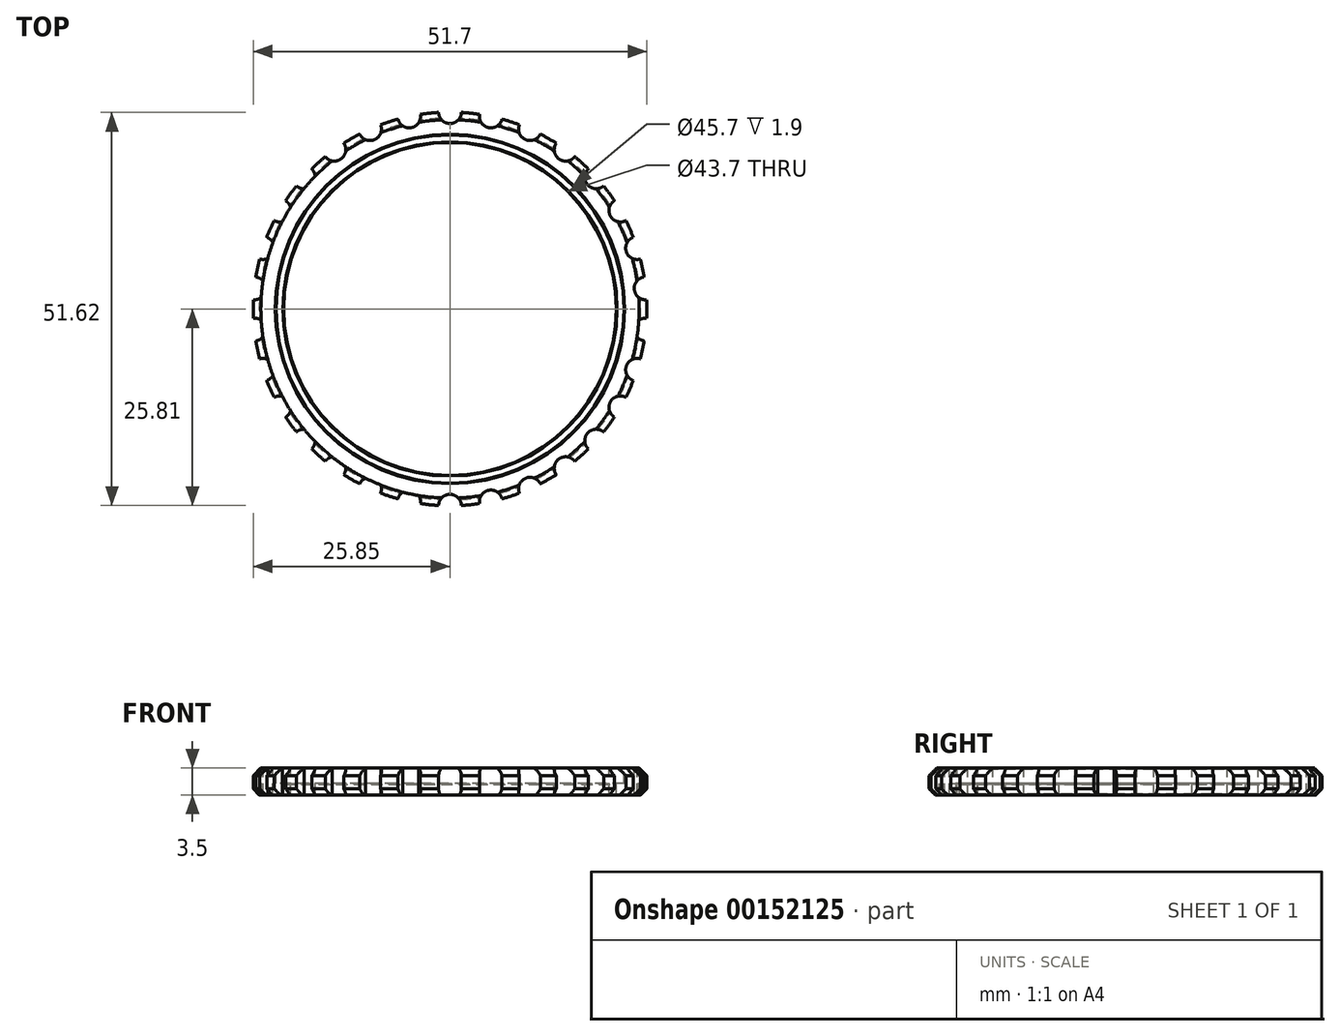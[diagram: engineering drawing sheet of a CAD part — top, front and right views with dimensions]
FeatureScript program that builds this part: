
annotation { "Feature Type Name" : "Feature", "Feature Type Description" : "" }
export const myFeature = defineFeature(function(context is Context, id is Id, definition is map)
    precondition{}
    {
        {
            var Q0;
            Q0=qCreatedBy(makeId("Front.planeOp"),FACE);
            var sketch = newSketch(context, id + "F0", { "sketchPlane" : qUnion([Q0])});
            skLineSegment(sketch, "E0.bottom", {"start": v(-22.85, -1) * mm, "end": v(22.85, -1) * mm, "construction": true});
            skLineSegment(sketch, "E0.top", {"start": v(-22.85, 1) * mm, "end": v(22.85, 1) * mm, "construction": true});
            skLineSegment(sketch, "E0.left", {"start": v(-22.85, -1) * mm, "end": v(-22.85, 1) * mm, "construction": true});
            skLineSegment(sketch, "E0.right", {"start": v(22.85, -1) * mm, "end": v(22.85, 1) * mm, "construction": true});
            skPoint(sketch, "E0.middle", {"position": v(0, 0) * mm});
            skLineSegment(sketch, "E1", {"start": v(-22.85, 1) * mm, "end": v(-25.85, 1) * mm});
            skLineSegment(sketch, "E2", {"start": v(-25.85, 1) * mm, "end": v(-25.85, -2.5) * mm});
            skLineSegment(sketch, "E3", {"start": v(-25.85, -2.5) * mm, "end": v(-21.85, -2.5) * mm});
            skLineSegment(sketch, "E4", {"start": v(-22.85, -1) * mm, "end": v(-21.85, -1) * mm});
            skLineSegment(sketch, "E5", {"start": v(-22.85, -1) * mm, "end": v(-22.85, 1) * mm});
            skLineSegment(sketch, "E6", {"start": v(-21.85, -1) * mm, "end": v(-21.85, -2.5) * mm});
            skLineSegment(sketch, "E7", {"start": v(0, 1) * mm, "end": v(0, -1) * mm, "construction": true});
            skSolve(sketch);
        }
        {
            var Q0;
            Q0=makeQuery(id+"F0.imprint","IMPRINT",FACE,{"disambiguationData":[TD([[makeQuery(id+"F0.imprint","IMPRINT",EDGE,{"derivedFrom":sQuery(id+"F0.wireOp",EDGE,"E1")}),1.0]])]});
            var Q1;
            Q1=sQuery(id+"F0.wireOp",EDGE,"E7");
            revolve(context, id + "F1", {"entities" : qUnion([Q0]), "axis" : qUnion([Q1]), "revolveType" : RevolveType.FULL});
        }
        {
            var Q0;
            Q0=makeQuery(id+"F1.opRevolve","SWEPT_EDGE",EDGE,{"disambiguationData":[OSD([sQuery(id+"F0.wireOp",EDGE,"E1"),sQuery(id+"F0.wireOp",EDGE,"E2")])]});
            chamfer(context, id + "F2", {"entities" : qUnion([Q0]), "width" : 1 * mm, "tangentPropagation" : true});
        }
        {
            var Q0;
            Q0=makeQuery(id+"F1.opRevolve","SWEPT_EDGE",EDGE,{"disambiguationData":[OSD([sQuery(id+"F0.wireOp",EDGE,"E2"),sQuery(id+"F0.wireOp",EDGE,"E3")])]});
            chamfer(context, id + "F3", {"entities" : qUnion([Q0]), "width" : .8 * mm, "tangentPropagation" : true});
        }
        {
            var Q0;
            Q0=makeQuery(id+"F1.opRevolve","SWEPT_EDGE",EDGE,{"disambiguationData":[OSD([sQuery(id+"F0.wireOp",EDGE,"E1"),sQuery(id+"F0.wireOp",EDGE,"E5")])]});
            var Q1;
            Q1=makeQuery(id+"F1.opRevolve","SWEPT_EDGE",EDGE,{"disambiguationData":[OSD([sQuery(id+"F0.wireOp",EDGE,"E4"),sQuery(id+"F0.wireOp",EDGE,"E6")])]});
            var Q2;
            Q2=makeQuery(id+"F1.opRevolve","SWEPT_EDGE",EDGE,{"disambiguationData":[OSD([sQuery(id+"F0.wireOp",EDGE,"E3"),sQuery(id+"F0.wireOp",EDGE,"E6")])]});
            chamfer(context, id + "F4", {"entities" : qUnion([Q0, Q1, Q2]), "width" : .1 * mm, "tangentPropagation" : true});
        }
        {
            var Q0;
            Q0=makeQuery(id+"F1.opRevolve","SWEPT_FACE",FACE,{"disambiguationData":[OSD([sQuery(id+"F0.wireOp",EDGE,"E1")])]});
            var sketch = newSketch(context, id + "F5", { "sketchPlane" : qUnion([Q0])});
            skCircle(sketch, "E8.0", {"center": v(0, 0) * mm, "radius": 25.85 * mm});
            skLineSegment(sketch, "E9", {"start": v(0, 0) * mm, "end": v(0, 25.85) * mm, "construction": true});
            skCircle(sketch, "E10", {"center": v(0, 25.85) * mm, "radius": 1.5 * mm});
            skCircle(sketch, "E11.1.0", {"center": v(-5.37, 25.29) * mm, "radius": 1.5 * mm});
            skCircle(sketch, "E11.2.0", {"center": v(-10.51, 23.62) * mm, "radius": 1.5 * mm});
            skCircle(sketch, "E11.3.0", {"center": v(-15.2, 20.91) * mm, "radius": 1.5 * mm});
            skCircle(sketch, "E11.4.0", {"center": v(-19.21, 17.3) * mm, "radius": 1.5 * mm});
            skCircle(sketch, "E11.5.0", {"center": v(-22.39, 12.93) * mm, "radius": 1.5 * mm});
            skCircle(sketch, "E11.6.0", {"center": v(-24.58, 7.99) * mm, "radius": 1.5 * mm});
            skCircle(sketch, "E11.7.0", {"center": v(-25.7, 2.7) * mm, "radius": 1.5 * mm});
            skCircle(sketch, "E11.8.0", {"center": v(-25.7, -2.7) * mm, "radius": 1.5 * mm});
            skCircle(sketch, "E11.9.0", {"center": v(-24.58, -7.99) * mm, "radius": 1.5 * mm});
            skCircle(sketch, "E11.10.0", {"center": v(-22.39, -12.92) * mm, "radius": 1.5 * mm});
            skCircle(sketch, "E11.11.0", {"center": v(-19.21, -17.3) * mm, "radius": 1.5 * mm});
            skCircle(sketch, "E11.12.0", {"center": v(-15.2, -20.91) * mm, "radius": 1.5 * mm});
            skCircle(sketch, "E11.13.0", {"center": v(-10.51, -23.62) * mm, "radius": 1.5 * mm});
            skCircle(sketch, "E11.14.0", {"center": v(-5.37, -25.29) * mm, "radius": 1.5 * mm});
            skCircle(sketch, "E11.15.0", {"center": v(0, -25.85) * mm, "radius": 1.5 * mm});
            skCircle(sketch, "E11.16.0", {"center": v(5.37, -25.29) * mm, "radius": 1.5 * mm});
            skCircle(sketch, "E11.17.0", {"center": v(10.51, -23.62) * mm, "radius": 1.5 * mm});
            skCircle(sketch, "E11.18.0", {"center": v(15.2, -20.91) * mm, "radius": 1.5 * mm});
            skCircle(sketch, "E11.19.0", {"center": v(19.21, -17.3) * mm, "radius": 1.5 * mm});
            skCircle(sketch, "E11.20.0", {"center": v(22.39, -12.93) * mm, "radius": 1.5 * mm});
            skCircle(sketch, "E11.21.0", {"center": v(24.58, -7.99) * mm, "radius": 1.5 * mm});
            skCircle(sketch, "E11.22.0", {"center": v(25.7, -2.7) * mm, "radius": 1.5 * mm});
            skCircle(sketch, "E11.23.0", {"center": v(25.7, 2.7) * mm, "radius": 1.5 * mm});
            skCircle(sketch, "E11.24.0", {"center": v(24.58, 7.99) * mm, "radius": 1.5 * mm});
            skCircle(sketch, "E11.25.0", {"center": v(22.39, 12.93) * mm, "radius": 1.5 * mm});
            skCircle(sketch, "E11.26.0", {"center": v(19.21, 17.3) * mm, "radius": 1.5 * mm});
            skCircle(sketch, "E11.27.0", {"center": v(15.2, 20.91) * mm, "radius": 1.5 * mm});
            skCircle(sketch, "E11.28.0", {"center": v(10.51, 23.62) * mm, "radius": 1.5 * mm});
            skCircle(sketch, "E11.29.0", {"center": v(5.37, 25.29) * mm, "radius": 1.5 * mm});
            skSolve(sketch);
        }
        {
            var Q0;
            {var subQ0=sQuery(id+"F5.wireOp",EDGE,"E10");var subQ1=sQuery(id+"F5.wireOp",EDGE,"E8.0");var subQ2=makeQuery(id+"F5.imprint","INTERSECT",VERTEX,{"disambiguationData":[OD(0.0)],"derivedFrom":[subQ1,subQ0]});Q0=makeQuery(id+"F5.imprint","IMPRINT",FACE,{"disambiguationData":[TD([[makeQuery(id+"F5.imprint","IMPRINT",EDGE,{"disambiguationData":[TD([[subQ2,-1.0]])],"derivedFrom":subQ1}),1.0]])]});}
            var Q1;
            {var subQ0=sQuery(id+"F5.wireOp",EDGE,"E10");var subQ1=sQuery(id+"F0.wireOp",EDGE,"E1");var subQ2=makeQuery(id+"F2.opChamfer","BLEND_EDGE",EDGE,{"blendedFrom":[makeQuery(id+"F1.opRevolve","SWEPT_EDGE",EDGE,{"disambiguationData":[OSD([subQ1,sQuery(id+"F0.wireOp",EDGE,"E2")])]}),makeQuery(id+"F1.opRevolve","SWEPT_FACE",FACE,{"disambiguationData":[OSD([subQ1])]})],"blendedInto":[makeQuery(id+"F1.opRevolve","SWEPT_FACE",FACE,{"disambiguationData":[OSD([subQ1])]})]});var subQ3=makeQuery(id+"F5.imprint","INTERSECT",VERTEX,{"disambiguationData":[OD(0.0)],"derivedFrom":[subQ2,subQ0]});Q1=makeQuery(id+"F5.imprint","IMPRINT",FACE,{"disambiguationData":[TD([[makeQuery(id+"F5.imprint","IMPRINT",EDGE,{"disambiguationData":[TD([[subQ3,-1.0]])],"derivedFrom":subQ0}),1.0]])]});}
            var Q2;
            {var subQ0=sQuery(id+"F5.wireOp",EDGE,"E11.29.0");var subQ1=sQuery(id+"F5.wireOp",EDGE,"E8.0");var subQ2=makeQuery(id+"F5.imprint","INTERSECT",VERTEX,{"disambiguationData":[OD(0.0)],"derivedFrom":[subQ1,subQ0]});Q2=makeQuery(id+"F5.imprint","IMPRINT",FACE,{"disambiguationData":[TD([[makeQuery(id+"F5.imprint","IMPRINT",EDGE,{"disambiguationData":[TD([[subQ2,-1.0]])],"derivedFrom":subQ1}),1.0]])]});}
            var Q3;
            {var subQ0=sQuery(id+"F5.wireOp",EDGE,"E11.29.0");var subQ1=sQuery(id+"F0.wireOp",EDGE,"E1");var subQ2=makeQuery(id+"F2.opChamfer","BLEND_EDGE",EDGE,{"blendedFrom":[makeQuery(id+"F1.opRevolve","SWEPT_EDGE",EDGE,{"disambiguationData":[OSD([subQ1,sQuery(id+"F0.wireOp",EDGE,"E2")])]}),makeQuery(id+"F1.opRevolve","SWEPT_FACE",FACE,{"disambiguationData":[OSD([subQ1])]})],"blendedInto":[makeQuery(id+"F1.opRevolve","SWEPT_FACE",FACE,{"disambiguationData":[OSD([subQ1])]})]});var subQ3=makeQuery(id+"F5.imprint","INTERSECT",VERTEX,{"disambiguationData":[OD(0.0)],"derivedFrom":[subQ2,subQ0]});Q3=makeQuery(id+"F5.imprint","IMPRINT",FACE,{"disambiguationData":[TD([[makeQuery(id+"F5.imprint","IMPRINT",EDGE,{"disambiguationData":[TD([[subQ3,-1.0]])],"derivedFrom":subQ0}),1.0]])]});}
            var Q4;
            {var subQ0=sQuery(id+"F5.wireOp",EDGE,"E11.28.0");var subQ1=sQuery(id+"F5.wireOp",EDGE,"E8.0");var subQ2=makeQuery(id+"F5.imprint","INTERSECT",VERTEX,{"disambiguationData":[OD(0.0)],"derivedFrom":[subQ1,subQ0]});Q4=makeQuery(id+"F5.imprint","IMPRINT",FACE,{"disambiguationData":[TD([[makeQuery(id+"F5.imprint","IMPRINT",EDGE,{"disambiguationData":[TD([[subQ2,-1.0]])],"derivedFrom":subQ1}),1.0]])]});}
            var Q5;
            {var subQ0=sQuery(id+"F5.wireOp",EDGE,"E11.27.0");var subQ1=sQuery(id+"F5.wireOp",EDGE,"E8.0");var subQ2=makeQuery(id+"F5.imprint","INTERSECT",VERTEX,{"disambiguationData":[OD(0.0)],"derivedFrom":[subQ1,subQ0]});Q5=makeQuery(id+"F5.imprint","IMPRINT",FACE,{"disambiguationData":[TD([[makeQuery(id+"F5.imprint","IMPRINT",EDGE,{"disambiguationData":[TD([[subQ2,-1.0]])],"derivedFrom":subQ1}),1.0]])]});}
            var Q6;
            {var subQ0=sQuery(id+"F5.wireOp",EDGE,"E11.28.0");var subQ1=sQuery(id+"F0.wireOp",EDGE,"E1");var subQ2=makeQuery(id+"F2.opChamfer","BLEND_EDGE",EDGE,{"blendedFrom":[makeQuery(id+"F1.opRevolve","SWEPT_EDGE",EDGE,{"disambiguationData":[OSD([subQ1,sQuery(id+"F0.wireOp",EDGE,"E2")])]}),makeQuery(id+"F1.opRevolve","SWEPT_FACE",FACE,{"disambiguationData":[OSD([subQ1])]})],"blendedInto":[makeQuery(id+"F1.opRevolve","SWEPT_FACE",FACE,{"disambiguationData":[OSD([subQ1])]})]});var subQ3=makeQuery(id+"F5.imprint","INTERSECT",VERTEX,{"disambiguationData":[OD(0.0)],"derivedFrom":[subQ2,subQ0]});Q6=makeQuery(id+"F5.imprint","IMPRINT",FACE,{"disambiguationData":[TD([[makeQuery(id+"F5.imprint","IMPRINT",EDGE,{"disambiguationData":[TD([[subQ3,-1.0]])],"derivedFrom":subQ0}),1.0]])]});}
            var Q7;
            {var subQ0=sQuery(id+"F5.wireOp",EDGE,"E11.27.0");var subQ1=sQuery(id+"F0.wireOp",EDGE,"E1");var subQ2=makeQuery(id+"F2.opChamfer","BLEND_EDGE",EDGE,{"blendedFrom":[makeQuery(id+"F1.opRevolve","SWEPT_EDGE",EDGE,{"disambiguationData":[OSD([subQ1,sQuery(id+"F0.wireOp",EDGE,"E2")])]}),makeQuery(id+"F1.opRevolve","SWEPT_FACE",FACE,{"disambiguationData":[OSD([subQ1])]})],"blendedInto":[makeQuery(id+"F1.opRevolve","SWEPT_FACE",FACE,{"disambiguationData":[OSD([subQ1])]})]});var subQ3=makeQuery(id+"F5.imprint","INTERSECT",VERTEX,{"disambiguationData":[OD(0.0)],"derivedFrom":[subQ2,subQ0]});Q7=makeQuery(id+"F5.imprint","IMPRINT",FACE,{"disambiguationData":[TD([[makeQuery(id+"F5.imprint","IMPRINT",EDGE,{"disambiguationData":[TD([[subQ3,-1.0]])],"derivedFrom":subQ0}),1.0]])]});}
            var Q8;
            {var subQ0=sQuery(id+"F5.wireOp",EDGE,"E11.26.0");var subQ1=sQuery(id+"F5.wireOp",EDGE,"E8.0");var subQ2=makeQuery(id+"F5.imprint","INTERSECT",VERTEX,{"disambiguationData":[OD(0.0)],"derivedFrom":[subQ1,subQ0]});Q8=makeQuery(id+"F5.imprint","IMPRINT",FACE,{"disambiguationData":[TD([[makeQuery(id+"F5.imprint","IMPRINT",EDGE,{"disambiguationData":[TD([[subQ2,-1.0]])],"derivedFrom":subQ1}),1.0]])]});}
            var Q9;
            {var subQ0=sQuery(id+"F5.wireOp",EDGE,"E11.26.0");var subQ1=sQuery(id+"F0.wireOp",EDGE,"E1");var subQ2=makeQuery(id+"F2.opChamfer","BLEND_EDGE",EDGE,{"blendedFrom":[makeQuery(id+"F1.opRevolve","SWEPT_EDGE",EDGE,{"disambiguationData":[OSD([subQ1,sQuery(id+"F0.wireOp",EDGE,"E2")])]}),makeQuery(id+"F1.opRevolve","SWEPT_FACE",FACE,{"disambiguationData":[OSD([subQ1])]})],"blendedInto":[makeQuery(id+"F1.opRevolve","SWEPT_FACE",FACE,{"disambiguationData":[OSD([subQ1])]})]});var subQ3=makeQuery(id+"F5.imprint","INTERSECT",VERTEX,{"disambiguationData":[OD(0.0)],"derivedFrom":[subQ2,subQ0]});Q9=makeQuery(id+"F5.imprint","IMPRINT",FACE,{"disambiguationData":[TD([[makeQuery(id+"F5.imprint","IMPRINT",EDGE,{"disambiguationData":[TD([[subQ3,-1.0]])],"derivedFrom":subQ0}),1.0]])]});}
            var Q10;
            {var subQ0=sQuery(id+"F5.wireOp",EDGE,"E11.25.0");var subQ1=sQuery(id+"F5.wireOp",EDGE,"E8.0");var subQ2=makeQuery(id+"F5.imprint","INTERSECT",VERTEX,{"disambiguationData":[OD(0.0)],"derivedFrom":[subQ1,subQ0]});Q10=makeQuery(id+"F5.imprint","IMPRINT",FACE,{"disambiguationData":[TD([[makeQuery(id+"F5.imprint","IMPRINT",EDGE,{"disambiguationData":[TD([[subQ2,-1.0]])],"derivedFrom":subQ1}),1.0]])]});}
            var Q11;
            {var subQ0=sQuery(id+"F5.wireOp",EDGE,"E11.25.0");var subQ1=sQuery(id+"F0.wireOp",EDGE,"E1");var subQ2=makeQuery(id+"F2.opChamfer","BLEND_EDGE",EDGE,{"blendedFrom":[makeQuery(id+"F1.opRevolve","SWEPT_EDGE",EDGE,{"disambiguationData":[OSD([subQ1,sQuery(id+"F0.wireOp",EDGE,"E2")])]}),makeQuery(id+"F1.opRevolve","SWEPT_FACE",FACE,{"disambiguationData":[OSD([subQ1])]})],"blendedInto":[makeQuery(id+"F1.opRevolve","SWEPT_FACE",FACE,{"disambiguationData":[OSD([subQ1])]})]});var subQ3=makeQuery(id+"F5.imprint","INTERSECT",VERTEX,{"disambiguationData":[OD(0.0)],"derivedFrom":[subQ2,subQ0]});Q11=makeQuery(id+"F5.imprint","IMPRINT",FACE,{"disambiguationData":[TD([[makeQuery(id+"F5.imprint","IMPRINT",EDGE,{"disambiguationData":[TD([[subQ3,-1.0]])],"derivedFrom":subQ0}),1.0]])]});}
            var Q12;
            {var subQ0=sQuery(id+"F5.wireOp",EDGE,"E11.24.0");var subQ1=sQuery(id+"F5.wireOp",EDGE,"E8.0");var subQ2=makeQuery(id+"F5.imprint","INTERSECT",VERTEX,{"disambiguationData":[OD(0.0)],"derivedFrom":[subQ1,subQ0]});Q12=makeQuery(id+"F5.imprint","IMPRINT",FACE,{"disambiguationData":[TD([[makeQuery(id+"F5.imprint","IMPRINT",EDGE,{"disambiguationData":[TD([[subQ2,-1.0]])],"derivedFrom":subQ1}),1.0]])]});}
            var Q13;
            {var subQ0=sQuery(id+"F5.wireOp",EDGE,"E11.24.0");var subQ1=sQuery(id+"F0.wireOp",EDGE,"E1");var subQ2=makeQuery(id+"F2.opChamfer","BLEND_EDGE",EDGE,{"blendedFrom":[makeQuery(id+"F1.opRevolve","SWEPT_EDGE",EDGE,{"disambiguationData":[OSD([subQ1,sQuery(id+"F0.wireOp",EDGE,"E2")])]}),makeQuery(id+"F1.opRevolve","SWEPT_FACE",FACE,{"disambiguationData":[OSD([subQ1])]})],"blendedInto":[makeQuery(id+"F1.opRevolve","SWEPT_FACE",FACE,{"disambiguationData":[OSD([subQ1])]})]});var subQ3=makeQuery(id+"F5.imprint","INTERSECT",VERTEX,{"disambiguationData":[OD(0.0)],"derivedFrom":[subQ2,subQ0]});Q13=makeQuery(id+"F5.imprint","IMPRINT",FACE,{"disambiguationData":[TD([[makeQuery(id+"F5.imprint","IMPRINT",EDGE,{"disambiguationData":[TD([[subQ3,-1.0]])],"derivedFrom":subQ0}),1.0]])]});}
            var Q14;
            {var subQ0=sQuery(id+"F5.wireOp",EDGE,"E11.23.0");var subQ1=sQuery(id+"F5.wireOp",EDGE,"E8.0");var subQ2=makeQuery(id+"F5.imprint","INTERSECT",VERTEX,{"disambiguationData":[OD(0.0)],"derivedFrom":[subQ1,subQ0]});Q14=makeQuery(id+"F5.imprint","IMPRINT",FACE,{"disambiguationData":[TD([[makeQuery(id+"F5.imprint","IMPRINT",EDGE,{"disambiguationData":[TD([[subQ2,1.0]])],"derivedFrom":subQ1}),1.0]])]});}
            var Q15;
            {var subQ0=sQuery(id+"F5.wireOp",EDGE,"E11.23.0");var subQ1=sQuery(id+"F0.wireOp",EDGE,"E1");var subQ2=makeQuery(id+"F2.opChamfer","BLEND_EDGE",EDGE,{"blendedFrom":[makeQuery(id+"F1.opRevolve","SWEPT_EDGE",EDGE,{"disambiguationData":[OSD([subQ1,sQuery(id+"F0.wireOp",EDGE,"E2")])]}),makeQuery(id+"F1.opRevolve","SWEPT_FACE",FACE,{"disambiguationData":[OSD([subQ1])]})],"blendedInto":[makeQuery(id+"F1.opRevolve","SWEPT_FACE",FACE,{"disambiguationData":[OSD([subQ1])]})]});var subQ3=makeQuery(id+"F5.imprint","INTERSECT",VERTEX,{"disambiguationData":[OD(0.0)],"derivedFrom":[subQ2,subQ0]});Q15=makeQuery(id+"F5.imprint","IMPRINT",FACE,{"disambiguationData":[TD([[makeQuery(id+"F5.imprint","IMPRINT",EDGE,{"disambiguationData":[TD([[subQ3,-1.0]])],"derivedFrom":subQ0}),1.0]])]});}
            var Q16;
            {var subQ0=sQuery(id+"F5.wireOp",EDGE,"E11.1.0");var subQ1=sQuery(id+"F5.wireOp",EDGE,"E8.0");var subQ2=makeQuery(id+"F5.imprint","INTERSECT",VERTEX,{"disambiguationData":[OD(0.0)],"derivedFrom":[subQ1,subQ0]});Q16=makeQuery(id+"F5.imprint","IMPRINT",FACE,{"disambiguationData":[TD([[makeQuery(id+"F5.imprint","IMPRINT",EDGE,{"disambiguationData":[TD([[subQ2,-1.0]])],"derivedFrom":subQ1}),1.0]])]});}
            var Q17;
            {var subQ0=sQuery(id+"F5.wireOp",EDGE,"E11.1.0");var subQ1=sQuery(id+"F0.wireOp",EDGE,"E1");var subQ2=makeQuery(id+"F2.opChamfer","BLEND_EDGE",EDGE,{"blendedFrom":[makeQuery(id+"F1.opRevolve","SWEPT_EDGE",EDGE,{"disambiguationData":[OSD([subQ1,sQuery(id+"F0.wireOp",EDGE,"E2")])]}),makeQuery(id+"F1.opRevolve","SWEPT_FACE",FACE,{"disambiguationData":[OSD([subQ1])]})],"blendedInto":[makeQuery(id+"F1.opRevolve","SWEPT_FACE",FACE,{"disambiguationData":[OSD([subQ1])]})]});var subQ3=makeQuery(id+"F5.imprint","INTERSECT",VERTEX,{"disambiguationData":[OD(0.0)],"derivedFrom":[subQ2,subQ0]});Q17=makeQuery(id+"F5.imprint","IMPRINT",FACE,{"disambiguationData":[TD([[makeQuery(id+"F5.imprint","IMPRINT",EDGE,{"disambiguationData":[TD([[subQ3,-1.0]])],"derivedFrom":subQ0}),1.0]])]});}
            var Q18;
            {var subQ0=sQuery(id+"F5.wireOp",EDGE,"E11.2.0");var subQ1=sQuery(id+"F5.wireOp",EDGE,"E8.0");var subQ2=makeQuery(id+"F5.imprint","INTERSECT",VERTEX,{"disambiguationData":[OD(0.0)],"derivedFrom":[subQ1,subQ0]});Q18=makeQuery(id+"F5.imprint","IMPRINT",FACE,{"disambiguationData":[TD([[makeQuery(id+"F5.imprint","IMPRINT",EDGE,{"disambiguationData":[TD([[subQ2,-1.0]])],"derivedFrom":subQ1}),1.0]])]});}
            var Q19;
            {var subQ0=sQuery(id+"F5.wireOp",EDGE,"E11.2.0");var subQ1=sQuery(id+"F0.wireOp",EDGE,"E1");var subQ2=makeQuery(id+"F2.opChamfer","BLEND_EDGE",EDGE,{"blendedFrom":[makeQuery(id+"F1.opRevolve","SWEPT_EDGE",EDGE,{"disambiguationData":[OSD([subQ1,sQuery(id+"F0.wireOp",EDGE,"E2")])]}),makeQuery(id+"F1.opRevolve","SWEPT_FACE",FACE,{"disambiguationData":[OSD([subQ1])]})],"blendedInto":[makeQuery(id+"F1.opRevolve","SWEPT_FACE",FACE,{"disambiguationData":[OSD([subQ1])]})]});var subQ3=makeQuery(id+"F5.imprint","INTERSECT",VERTEX,{"disambiguationData":[OD(0.0)],"derivedFrom":[subQ2,subQ0]});Q19=makeQuery(id+"F5.imprint","IMPRINT",FACE,{"disambiguationData":[TD([[makeQuery(id+"F5.imprint","IMPRINT",EDGE,{"disambiguationData":[TD([[subQ3,-1.0]])],"derivedFrom":subQ0}),1.0]])]});}
            var Q20;
            {var subQ0=sQuery(id+"F5.wireOp",EDGE,"E11.3.0");var subQ1=sQuery(id+"F5.wireOp",EDGE,"E8.0");var subQ2=makeQuery(id+"F5.imprint","INTERSECT",VERTEX,{"disambiguationData":[OD(0.0)],"derivedFrom":[subQ1,subQ0]});Q20=makeQuery(id+"F5.imprint","IMPRINT",FACE,{"disambiguationData":[TD([[makeQuery(id+"F5.imprint","IMPRINT",EDGE,{"disambiguationData":[TD([[subQ2,-1.0]])],"derivedFrom":subQ1}),1.0]])]});}
            var Q21;
            {var subQ0=sQuery(id+"F5.wireOp",EDGE,"E11.3.0");var subQ1=sQuery(id+"F0.wireOp",EDGE,"E1");var subQ2=makeQuery(id+"F2.opChamfer","BLEND_EDGE",EDGE,{"blendedFrom":[makeQuery(id+"F1.opRevolve","SWEPT_EDGE",EDGE,{"disambiguationData":[OSD([subQ1,sQuery(id+"F0.wireOp",EDGE,"E2")])]}),makeQuery(id+"F1.opRevolve","SWEPT_FACE",FACE,{"disambiguationData":[OSD([subQ1])]})],"blendedInto":[makeQuery(id+"F1.opRevolve","SWEPT_FACE",FACE,{"disambiguationData":[OSD([subQ1])]})]});var subQ3=makeQuery(id+"F5.imprint","INTERSECT",VERTEX,{"disambiguationData":[OD(0.0)],"derivedFrom":[subQ2,subQ0]});Q21=makeQuery(id+"F5.imprint","IMPRINT",FACE,{"disambiguationData":[TD([[makeQuery(id+"F5.imprint","IMPRINT",EDGE,{"disambiguationData":[TD([[subQ3,-1.0]])],"derivedFrom":subQ0}),1.0]])]});}
            var Q22;
            {var subQ0=sQuery(id+"F5.wireOp",EDGE,"E11.4.0");var subQ1=sQuery(id+"F5.wireOp",EDGE,"E8.0");var subQ2=makeQuery(id+"F5.imprint","INTERSECT",VERTEX,{"disambiguationData":[OD(0.0)],"derivedFrom":[subQ1,subQ0]});Q22=makeQuery(id+"F5.imprint","IMPRINT",FACE,{"disambiguationData":[TD([[makeQuery(id+"F5.imprint","IMPRINT",EDGE,{"disambiguationData":[TD([[subQ2,-1.0]])],"derivedFrom":subQ1}),1.0]])]});}
            var Q23;
            {var subQ0=sQuery(id+"F5.wireOp",EDGE,"E11.4.0");var subQ1=sQuery(id+"F0.wireOp",EDGE,"E1");var subQ2=makeQuery(id+"F2.opChamfer","BLEND_EDGE",EDGE,{"blendedFrom":[makeQuery(id+"F1.opRevolve","SWEPT_EDGE",EDGE,{"disambiguationData":[OSD([subQ1,sQuery(id+"F0.wireOp",EDGE,"E2")])]}),makeQuery(id+"F1.opRevolve","SWEPT_FACE",FACE,{"disambiguationData":[OSD([subQ1])]})],"blendedInto":[makeQuery(id+"F1.opRevolve","SWEPT_FACE",FACE,{"disambiguationData":[OSD([subQ1])]})]});var subQ3=makeQuery(id+"F5.imprint","INTERSECT",VERTEX,{"disambiguationData":[OD(0.0)],"derivedFrom":[subQ2,subQ0]});Q23=makeQuery(id+"F5.imprint","IMPRINT",FACE,{"disambiguationData":[TD([[makeQuery(id+"F5.imprint","IMPRINT",EDGE,{"disambiguationData":[TD([[subQ3,-1.0]])],"derivedFrom":subQ0}),1.0]])]});}
            var Q24;
            {var subQ0=sQuery(id+"F5.wireOp",EDGE,"E11.5.0");var subQ1=sQuery(id+"F5.wireOp",EDGE,"E8.0");var subQ2=makeQuery(id+"F5.imprint","INTERSECT",VERTEX,{"disambiguationData":[OD(0.0)],"derivedFrom":[subQ1,subQ0]});Q24=makeQuery(id+"F5.imprint","IMPRINT",FACE,{"disambiguationData":[TD([[makeQuery(id+"F5.imprint","IMPRINT",EDGE,{"disambiguationData":[TD([[subQ2,-1.0]])],"derivedFrom":subQ1}),1.0]])]});}
            var Q25;
            {var subQ0=sQuery(id+"F5.wireOp",EDGE,"E11.5.0");var subQ1=sQuery(id+"F0.wireOp",EDGE,"E1");var subQ2=makeQuery(id+"F2.opChamfer","BLEND_EDGE",EDGE,{"blendedFrom":[makeQuery(id+"F1.opRevolve","SWEPT_EDGE",EDGE,{"disambiguationData":[OSD([subQ1,sQuery(id+"F0.wireOp",EDGE,"E2")])]}),makeQuery(id+"F1.opRevolve","SWEPT_FACE",FACE,{"disambiguationData":[OSD([subQ1])]})],"blendedInto":[makeQuery(id+"F1.opRevolve","SWEPT_FACE",FACE,{"disambiguationData":[OSD([subQ1])]})]});var subQ3=makeQuery(id+"F5.imprint","INTERSECT",VERTEX,{"disambiguationData":[OD(0.0)],"derivedFrom":[subQ2,subQ0]});Q25=makeQuery(id+"F5.imprint","IMPRINT",FACE,{"disambiguationData":[TD([[makeQuery(id+"F5.imprint","IMPRINT",EDGE,{"disambiguationData":[TD([[subQ3,-1.0]])],"derivedFrom":subQ0}),1.0]])]});}
            var Q26;
            {var subQ0=sQuery(id+"F5.wireOp",EDGE,"E11.6.0");var subQ1=sQuery(id+"F5.wireOp",EDGE,"E8.0");var subQ2=makeQuery(id+"F5.imprint","INTERSECT",VERTEX,{"disambiguationData":[OD(0.0)],"derivedFrom":[subQ1,subQ0]});Q26=makeQuery(id+"F5.imprint","IMPRINT",FACE,{"disambiguationData":[TD([[makeQuery(id+"F5.imprint","IMPRINT",EDGE,{"disambiguationData":[TD([[subQ2,-1.0]])],"derivedFrom":subQ1}),1.0]])]});}
            var Q27;
            {var subQ0=sQuery(id+"F5.wireOp",EDGE,"E11.6.0");var subQ1=sQuery(id+"F0.wireOp",EDGE,"E1");var subQ2=makeQuery(id+"F2.opChamfer","BLEND_EDGE",EDGE,{"blendedFrom":[makeQuery(id+"F1.opRevolve","SWEPT_EDGE",EDGE,{"disambiguationData":[OSD([subQ1,sQuery(id+"F0.wireOp",EDGE,"E2")])]}),makeQuery(id+"F1.opRevolve","SWEPT_FACE",FACE,{"disambiguationData":[OSD([subQ1])]})],"blendedInto":[makeQuery(id+"F1.opRevolve","SWEPT_FACE",FACE,{"disambiguationData":[OSD([subQ1])]})]});var subQ3=makeQuery(id+"F5.imprint","INTERSECT",VERTEX,{"disambiguationData":[OD(0.0)],"derivedFrom":[subQ2,subQ0]});Q27=makeQuery(id+"F5.imprint","IMPRINT",FACE,{"disambiguationData":[TD([[makeQuery(id+"F5.imprint","IMPRINT",EDGE,{"disambiguationData":[TD([[subQ3,-1.0]])],"derivedFrom":subQ0}),1.0]])]});}
            var Q28;
            {var subQ0=sQuery(id+"F5.wireOp",EDGE,"E11.7.0");var subQ1=sQuery(id+"F5.wireOp",EDGE,"E8.0");var subQ2=makeQuery(id+"F5.imprint","INTERSECT",VERTEX,{"disambiguationData":[OD(0.0)],"derivedFrom":[subQ1,subQ0]});Q28=makeQuery(id+"F5.imprint","IMPRINT",FACE,{"disambiguationData":[TD([[makeQuery(id+"F5.imprint","IMPRINT",EDGE,{"disambiguationData":[TD([[subQ2,-1.0]])],"derivedFrom":subQ1}),1.0]])]});}
            var Q29;
            {var subQ0=sQuery(id+"F5.wireOp",EDGE,"E11.7.0");var subQ1=sQuery(id+"F0.wireOp",EDGE,"E1");var subQ2=makeQuery(id+"F2.opChamfer","BLEND_EDGE",EDGE,{"blendedFrom":[makeQuery(id+"F1.opRevolve","SWEPT_EDGE",EDGE,{"disambiguationData":[OSD([subQ1,sQuery(id+"F0.wireOp",EDGE,"E2")])]}),makeQuery(id+"F1.opRevolve","SWEPT_FACE",FACE,{"disambiguationData":[OSD([subQ1])]})],"blendedInto":[makeQuery(id+"F1.opRevolve","SWEPT_FACE",FACE,{"disambiguationData":[OSD([subQ1])]})]});var subQ3=makeQuery(id+"F5.imprint","INTERSECT",VERTEX,{"disambiguationData":[OD(0.0)],"derivedFrom":[subQ2,subQ0]});Q29=makeQuery(id+"F5.imprint","IMPRINT",FACE,{"disambiguationData":[TD([[makeQuery(id+"F5.imprint","IMPRINT",EDGE,{"disambiguationData":[TD([[subQ3,-1.0]])],"derivedFrom":subQ0}),1.0]])]});}
            var Q30;
            {var subQ0=sQuery(id+"F5.wireOp",EDGE,"E11.8.0");var subQ1=sQuery(id+"F5.wireOp",EDGE,"E8.0");var subQ2=makeQuery(id+"F5.imprint","INTERSECT",VERTEX,{"disambiguationData":[OD(0.0)],"derivedFrom":[subQ1,subQ0]});Q30=makeQuery(id+"F5.imprint","IMPRINT",FACE,{"disambiguationData":[TD([[makeQuery(id+"F5.imprint","IMPRINT",EDGE,{"disambiguationData":[TD([[subQ2,-1.0]])],"derivedFrom":subQ1}),1.0]])]});}
            var Q31;
            {var subQ0=sQuery(id+"F5.wireOp",EDGE,"E11.8.0");var subQ1=sQuery(id+"F0.wireOp",EDGE,"E1");var subQ2=makeQuery(id+"F2.opChamfer","BLEND_EDGE",EDGE,{"blendedFrom":[makeQuery(id+"F1.opRevolve","SWEPT_EDGE",EDGE,{"disambiguationData":[OSD([subQ1,sQuery(id+"F0.wireOp",EDGE,"E2")])]}),makeQuery(id+"F1.opRevolve","SWEPT_FACE",FACE,{"disambiguationData":[OSD([subQ1])]})],"blendedInto":[makeQuery(id+"F1.opRevolve","SWEPT_FACE",FACE,{"disambiguationData":[OSD([subQ1])]})]});var subQ3=makeQuery(id+"F5.imprint","INTERSECT",VERTEX,{"disambiguationData":[OD(0.0)],"derivedFrom":[subQ2,subQ0]});Q31=makeQuery(id+"F5.imprint","IMPRINT",FACE,{"disambiguationData":[TD([[makeQuery(id+"F5.imprint","IMPRINT",EDGE,{"disambiguationData":[TD([[subQ3,-1.0]])],"derivedFrom":subQ0}),1.0]])]});}
            var Q32;
            {var subQ0=sQuery(id+"F5.wireOp",EDGE,"E11.9.0");var subQ1=sQuery(id+"F5.wireOp",EDGE,"E8.0");var subQ2=makeQuery(id+"F5.imprint","INTERSECT",VERTEX,{"disambiguationData":[OD(0.0)],"derivedFrom":[subQ1,subQ0]});Q32=makeQuery(id+"F5.imprint","IMPRINT",FACE,{"disambiguationData":[TD([[makeQuery(id+"F5.imprint","IMPRINT",EDGE,{"disambiguationData":[TD([[subQ2,-1.0]])],"derivedFrom":subQ1}),1.0]])]});}
            var Q33;
            {var subQ0=sQuery(id+"F5.wireOp",EDGE,"E11.9.0");var subQ1=sQuery(id+"F0.wireOp",EDGE,"E1");var subQ2=makeQuery(id+"F2.opChamfer","BLEND_EDGE",EDGE,{"blendedFrom":[makeQuery(id+"F1.opRevolve","SWEPT_EDGE",EDGE,{"disambiguationData":[OSD([subQ1,sQuery(id+"F0.wireOp",EDGE,"E2")])]}),makeQuery(id+"F1.opRevolve","SWEPT_FACE",FACE,{"disambiguationData":[OSD([subQ1])]})],"blendedInto":[makeQuery(id+"F1.opRevolve","SWEPT_FACE",FACE,{"disambiguationData":[OSD([subQ1])]})]});var subQ3=makeQuery(id+"F5.imprint","INTERSECT",VERTEX,{"disambiguationData":[OD(0.0)],"derivedFrom":[subQ2,subQ0]});Q33=makeQuery(id+"F5.imprint","IMPRINT",FACE,{"disambiguationData":[TD([[makeQuery(id+"F5.imprint","IMPRINT",EDGE,{"disambiguationData":[TD([[subQ3,-1.0]])],"derivedFrom":subQ0}),1.0]])]});}
            var Q34;
            {var subQ0=sQuery(id+"F5.wireOp",EDGE,"E11.10.0");var subQ1=sQuery(id+"F5.wireOp",EDGE,"E8.0");var subQ2=makeQuery(id+"F5.imprint","INTERSECT",VERTEX,{"disambiguationData":[OD(0.0)],"derivedFrom":[subQ1,subQ0]});Q34=makeQuery(id+"F5.imprint","IMPRINT",FACE,{"disambiguationData":[TD([[makeQuery(id+"F5.imprint","IMPRINT",EDGE,{"disambiguationData":[TD([[subQ2,-1.0]])],"derivedFrom":subQ1}),1.0]])]});}
            var Q35;
            {var subQ0=sQuery(id+"F5.wireOp",EDGE,"E11.10.0");var subQ1=sQuery(id+"F0.wireOp",EDGE,"E1");var subQ2=makeQuery(id+"F2.opChamfer","BLEND_EDGE",EDGE,{"blendedFrom":[makeQuery(id+"F1.opRevolve","SWEPT_EDGE",EDGE,{"disambiguationData":[OSD([subQ1,sQuery(id+"F0.wireOp",EDGE,"E2")])]}),makeQuery(id+"F1.opRevolve","SWEPT_FACE",FACE,{"disambiguationData":[OSD([subQ1])]})],"blendedInto":[makeQuery(id+"F1.opRevolve","SWEPT_FACE",FACE,{"disambiguationData":[OSD([subQ1])]})]});var subQ3=makeQuery(id+"F5.imprint","INTERSECT",VERTEX,{"disambiguationData":[OD(0.0)],"derivedFrom":[subQ2,subQ0]});Q35=makeQuery(id+"F5.imprint","IMPRINT",FACE,{"disambiguationData":[TD([[makeQuery(id+"F5.imprint","IMPRINT",EDGE,{"disambiguationData":[TD([[subQ3,-1.0]])],"derivedFrom":subQ0}),1.0]])]});}
            var Q36;
            {var subQ0=sQuery(id+"F5.wireOp",EDGE,"E11.11.0");var subQ1=sQuery(id+"F0.wireOp",EDGE,"E1");var subQ2=makeQuery(id+"F2.opChamfer","BLEND_EDGE",EDGE,{"blendedFrom":[makeQuery(id+"F1.opRevolve","SWEPT_EDGE",EDGE,{"disambiguationData":[OSD([subQ1,sQuery(id+"F0.wireOp",EDGE,"E2")])]}),makeQuery(id+"F1.opRevolve","SWEPT_FACE",FACE,{"disambiguationData":[OSD([subQ1])]})],"blendedInto":[makeQuery(id+"F1.opRevolve","SWEPT_FACE",FACE,{"disambiguationData":[OSD([subQ1])]})]});var subQ3=makeQuery(id+"F5.imprint","INTERSECT",VERTEX,{"disambiguationData":[OD(0.0)],"derivedFrom":[subQ2,subQ0]});Q36=makeQuery(id+"F5.imprint","IMPRINT",FACE,{"disambiguationData":[TD([[makeQuery(id+"F5.imprint","IMPRINT",EDGE,{"disambiguationData":[TD([[subQ3,-1.0]])],"derivedFrom":subQ0}),1.0]])]});}
            var Q37;
            {var subQ0=sQuery(id+"F5.wireOp",EDGE,"E11.11.0");var subQ1=sQuery(id+"F5.wireOp",EDGE,"E8.0");var subQ2=makeQuery(id+"F5.imprint","INTERSECT",VERTEX,{"disambiguationData":[OD(0.0)],"derivedFrom":[subQ1,subQ0]});Q37=makeQuery(id+"F5.imprint","IMPRINT",FACE,{"disambiguationData":[TD([[makeQuery(id+"F5.imprint","IMPRINT",EDGE,{"disambiguationData":[TD([[subQ2,-1.0]])],"derivedFrom":subQ1}),1.0]])]});}
            var Q38;
            {var subQ0=sQuery(id+"F5.wireOp",EDGE,"E11.12.0");var subQ1=sQuery(id+"F5.wireOp",EDGE,"E8.0");var subQ2=makeQuery(id+"F5.imprint","INTERSECT",VERTEX,{"disambiguationData":[OD(0.0)],"derivedFrom":[subQ1,subQ0]});Q38=makeQuery(id+"F5.imprint","IMPRINT",FACE,{"disambiguationData":[TD([[makeQuery(id+"F5.imprint","IMPRINT",EDGE,{"disambiguationData":[TD([[subQ2,-1.0]])],"derivedFrom":subQ1}),1.0]])]});}
            var Q39;
            {var subQ0=sQuery(id+"F5.wireOp",EDGE,"E11.12.0");var subQ1=sQuery(id+"F0.wireOp",EDGE,"E1");var subQ2=makeQuery(id+"F2.opChamfer","BLEND_EDGE",EDGE,{"blendedFrom":[makeQuery(id+"F1.opRevolve","SWEPT_EDGE",EDGE,{"disambiguationData":[OSD([subQ1,sQuery(id+"F0.wireOp",EDGE,"E2")])]}),makeQuery(id+"F1.opRevolve","SWEPT_FACE",FACE,{"disambiguationData":[OSD([subQ1])]})],"blendedInto":[makeQuery(id+"F1.opRevolve","SWEPT_FACE",FACE,{"disambiguationData":[OSD([subQ1])]})]});var subQ3=makeQuery(id+"F5.imprint","INTERSECT",VERTEX,{"disambiguationData":[OD(0.0)],"derivedFrom":[subQ2,subQ0]});Q39=makeQuery(id+"F5.imprint","IMPRINT",FACE,{"disambiguationData":[TD([[makeQuery(id+"F5.imprint","IMPRINT",EDGE,{"disambiguationData":[TD([[subQ3,-1.0]])],"derivedFrom":subQ0}),1.0]])]});}
            var Q40;
            {var subQ0=sQuery(id+"F5.wireOp",EDGE,"E11.18.0");var subQ1=sQuery(id+"F5.wireOp",EDGE,"E8.0");var subQ2=makeQuery(id+"F5.imprint","INTERSECT",VERTEX,{"disambiguationData":[OD(0.0)],"derivedFrom":[subQ1,subQ0]});Q40=makeQuery(id+"F5.imprint","IMPRINT",FACE,{"disambiguationData":[TD([[makeQuery(id+"F5.imprint","IMPRINT",EDGE,{"disambiguationData":[TD([[subQ2,-1.0]])],"derivedFrom":subQ1}),1.0]])]});}
            var Q41;
            {var subQ0=sQuery(id+"F5.wireOp",EDGE,"E11.18.0");var subQ1=sQuery(id+"F0.wireOp",EDGE,"E1");var subQ2=makeQuery(id+"F2.opChamfer","BLEND_EDGE",EDGE,{"blendedFrom":[makeQuery(id+"F1.opRevolve","SWEPT_EDGE",EDGE,{"disambiguationData":[OSD([subQ1,sQuery(id+"F0.wireOp",EDGE,"E2")])]}),makeQuery(id+"F1.opRevolve","SWEPT_FACE",FACE,{"disambiguationData":[OSD([subQ1])]})],"blendedInto":[makeQuery(id+"F1.opRevolve","SWEPT_FACE",FACE,{"disambiguationData":[OSD([subQ1])]})]});var subQ3=makeQuery(id+"F5.imprint","INTERSECT",VERTEX,{"disambiguationData":[OD(0.0)],"derivedFrom":[subQ2,subQ0]});Q41=makeQuery(id+"F5.imprint","IMPRINT",FACE,{"disambiguationData":[TD([[makeQuery(id+"F5.imprint","IMPRINT",EDGE,{"disambiguationData":[TD([[subQ3,-1.0]])],"derivedFrom":subQ0}),1.0]])]});}
            var Q42;
            {var subQ0=sQuery(id+"F5.wireOp",EDGE,"E11.19.0");var subQ1=sQuery(id+"F5.wireOp",EDGE,"E8.0");var subQ2=makeQuery(id+"F5.imprint","INTERSECT",VERTEX,{"disambiguationData":[OD(0.0)],"derivedFrom":[subQ1,subQ0]});Q42=makeQuery(id+"F5.imprint","IMPRINT",FACE,{"disambiguationData":[TD([[makeQuery(id+"F5.imprint","IMPRINT",EDGE,{"disambiguationData":[TD([[subQ2,-1.0]])],"derivedFrom":subQ1}),1.0]])]});}
            var Q43;
            {var subQ0=sQuery(id+"F5.wireOp",EDGE,"E11.19.0");var subQ1=sQuery(id+"F0.wireOp",EDGE,"E1");var subQ2=makeQuery(id+"F2.opChamfer","BLEND_EDGE",EDGE,{"blendedFrom":[makeQuery(id+"F1.opRevolve","SWEPT_EDGE",EDGE,{"disambiguationData":[OSD([subQ1,sQuery(id+"F0.wireOp",EDGE,"E2")])]}),makeQuery(id+"F1.opRevolve","SWEPT_FACE",FACE,{"disambiguationData":[OSD([subQ1])]})],"blendedInto":[makeQuery(id+"F1.opRevolve","SWEPT_FACE",FACE,{"disambiguationData":[OSD([subQ1])]})]});var subQ3=makeQuery(id+"F5.imprint","INTERSECT",VERTEX,{"disambiguationData":[OD(0.0)],"derivedFrom":[subQ2,subQ0]});Q43=makeQuery(id+"F5.imprint","IMPRINT",FACE,{"disambiguationData":[TD([[makeQuery(id+"F5.imprint","IMPRINT",EDGE,{"disambiguationData":[TD([[subQ3,-1.0]])],"derivedFrom":subQ0}),1.0]])]});}
            var Q44;
            {var subQ0=sQuery(id+"F5.wireOp",EDGE,"E11.17.0");var subQ1=sQuery(id+"F5.wireOp",EDGE,"E8.0");var subQ2=makeQuery(id+"F5.imprint","INTERSECT",VERTEX,{"disambiguationData":[OD(0.0)],"derivedFrom":[subQ1,subQ0]});Q44=makeQuery(id+"F5.imprint","IMPRINT",FACE,{"disambiguationData":[TD([[makeQuery(id+"F5.imprint","IMPRINT",EDGE,{"disambiguationData":[TD([[subQ2,-1.0]])],"derivedFrom":subQ1}),1.0]])]});}
            var Q45;
            {var subQ0=sQuery(id+"F5.wireOp",EDGE,"E11.17.0");var subQ1=sQuery(id+"F0.wireOp",EDGE,"E1");var subQ2=makeQuery(id+"F2.opChamfer","BLEND_EDGE",EDGE,{"blendedFrom":[makeQuery(id+"F1.opRevolve","SWEPT_EDGE",EDGE,{"disambiguationData":[OSD([subQ1,sQuery(id+"F0.wireOp",EDGE,"E2")])]}),makeQuery(id+"F1.opRevolve","SWEPT_FACE",FACE,{"disambiguationData":[OSD([subQ1])]})],"blendedInto":[makeQuery(id+"F1.opRevolve","SWEPT_FACE",FACE,{"disambiguationData":[OSD([subQ1])]})]});var subQ3=makeQuery(id+"F5.imprint","INTERSECT",VERTEX,{"disambiguationData":[OD(0.0)],"derivedFrom":[subQ2,subQ0]});Q45=makeQuery(id+"F5.imprint","IMPRINT",FACE,{"disambiguationData":[TD([[makeQuery(id+"F5.imprint","IMPRINT",EDGE,{"disambiguationData":[TD([[subQ3,-1.0]])],"derivedFrom":subQ0}),1.0]])]});}
            var Q46;
            {var subQ0=sQuery(id+"F5.wireOp",EDGE,"E11.20.0");var subQ1=sQuery(id+"F5.wireOp",EDGE,"E8.0");var subQ2=makeQuery(id+"F5.imprint","INTERSECT",VERTEX,{"disambiguationData":[OD(0.0)],"derivedFrom":[subQ1,subQ0]});Q46=makeQuery(id+"F5.imprint","IMPRINT",FACE,{"disambiguationData":[TD([[makeQuery(id+"F5.imprint","IMPRINT",EDGE,{"disambiguationData":[TD([[subQ2,-1.0]])],"derivedFrom":subQ1}),1.0]])]});}
            var Q47;
            {var subQ0=sQuery(id+"F5.wireOp",EDGE,"E11.20.0");var subQ1=sQuery(id+"F0.wireOp",EDGE,"E1");var subQ2=makeQuery(id+"F2.opChamfer","BLEND_EDGE",EDGE,{"blendedFrom":[makeQuery(id+"F1.opRevolve","SWEPT_EDGE",EDGE,{"disambiguationData":[OSD([subQ1,sQuery(id+"F0.wireOp",EDGE,"E2")])]}),makeQuery(id+"F1.opRevolve","SWEPT_FACE",FACE,{"disambiguationData":[OSD([subQ1])]})],"blendedInto":[makeQuery(id+"F1.opRevolve","SWEPT_FACE",FACE,{"disambiguationData":[OSD([subQ1])]})]});var subQ3=makeQuery(id+"F5.imprint","INTERSECT",VERTEX,{"disambiguationData":[OD(0.0)],"derivedFrom":[subQ2,subQ0]});Q47=makeQuery(id+"F5.imprint","IMPRINT",FACE,{"disambiguationData":[TD([[makeQuery(id+"F5.imprint","IMPRINT",EDGE,{"disambiguationData":[TD([[subQ3,-1.0]])],"derivedFrom":subQ0}),1.0]])]});}
            var Q48;
            {var subQ0=sQuery(id+"F5.wireOp",EDGE,"E11.21.0");var subQ1=sQuery(id+"F5.wireOp",EDGE,"E8.0");var subQ2=makeQuery(id+"F5.imprint","INTERSECT",VERTEX,{"disambiguationData":[OD(0.0)],"derivedFrom":[subQ1,subQ0]});Q48=makeQuery(id+"F5.imprint","IMPRINT",FACE,{"disambiguationData":[TD([[makeQuery(id+"F5.imprint","IMPRINT",EDGE,{"disambiguationData":[TD([[subQ2,-1.0]])],"derivedFrom":subQ1}),1.0]])]});}
            var Q49;
            {var subQ0=sQuery(id+"F5.wireOp",EDGE,"E11.21.0");var subQ1=sQuery(id+"F0.wireOp",EDGE,"E1");var subQ2=makeQuery(id+"F2.opChamfer","BLEND_EDGE",EDGE,{"blendedFrom":[makeQuery(id+"F1.opRevolve","SWEPT_EDGE",EDGE,{"disambiguationData":[OSD([subQ1,sQuery(id+"F0.wireOp",EDGE,"E2")])]}),makeQuery(id+"F1.opRevolve","SWEPT_FACE",FACE,{"disambiguationData":[OSD([subQ1])]})],"blendedInto":[makeQuery(id+"F1.opRevolve","SWEPT_FACE",FACE,{"disambiguationData":[OSD([subQ1])]})]});var subQ3=makeQuery(id+"F5.imprint","INTERSECT",VERTEX,{"disambiguationData":[OD(0.0)],"derivedFrom":[subQ2,subQ0]});Q49=makeQuery(id+"F5.imprint","IMPRINT",FACE,{"disambiguationData":[TD([[makeQuery(id+"F5.imprint","IMPRINT",EDGE,{"disambiguationData":[TD([[subQ3,-1.0]])],"derivedFrom":subQ0}),1.0]])]});}
            var Q50;
            {var subQ0=sQuery(id+"F5.wireOp",EDGE,"E11.22.0");var subQ1=sQuery(id+"F5.wireOp",EDGE,"E8.0");var subQ2=makeQuery(id+"F5.imprint","INTERSECT",VERTEX,{"disambiguationData":[OD(0.0)],"derivedFrom":[subQ1,subQ0]});Q50=makeQuery(id+"F5.imprint","IMPRINT",FACE,{"disambiguationData":[TD([[makeQuery(id+"F5.imprint","IMPRINT",EDGE,{"disambiguationData":[TD([[subQ2,-1.0]])],"derivedFrom":subQ1}),1.0]])]});}
            var Q51;
            {var subQ0=sQuery(id+"F5.wireOp",EDGE,"E11.22.0");var subQ1=sQuery(id+"F5.wireOp",EDGE,"E8.0");var subQ2=makeQuery(id+"F5.imprint","INTERSECT",VERTEX,{"disambiguationData":[OD(0.0)],"derivedFrom":[subQ1,subQ0]});Q51=makeQuery(id+"F5.imprint","IMPRINT",FACE,{"disambiguationData":[TD([[makeQuery(id+"F5.imprint","IMPRINT",EDGE,{"disambiguationData":[TD([[subQ2,-1.0]])],"derivedFrom":subQ1}),1.0]])]});}
            var Q52;
            {var subQ0=sQuery(id+"F5.wireOp",EDGE,"E11.13.0");var subQ1=sQuery(id+"F5.wireOp",EDGE,"E8.0");var subQ2=makeQuery(id+"F5.imprint","INTERSECT",VERTEX,{"disambiguationData":[OD(0.0)],"derivedFrom":[subQ1,subQ0]});Q52=makeQuery(id+"F5.imprint","IMPRINT",FACE,{"disambiguationData":[TD([[makeQuery(id+"F5.imprint","IMPRINT",EDGE,{"disambiguationData":[TD([[subQ2,-1.0]])],"derivedFrom":subQ1}),1.0]])]});}
            var Q53;
            {var subQ0=sQuery(id+"F5.wireOp",EDGE,"E11.13.0");var subQ1=sQuery(id+"F0.wireOp",EDGE,"E1");var subQ2=makeQuery(id+"F2.opChamfer","BLEND_EDGE",EDGE,{"blendedFrom":[makeQuery(id+"F1.opRevolve","SWEPT_EDGE",EDGE,{"disambiguationData":[OSD([subQ1,sQuery(id+"F0.wireOp",EDGE,"E2")])]}),makeQuery(id+"F1.opRevolve","SWEPT_FACE",FACE,{"disambiguationData":[OSD([subQ1])]})],"blendedInto":[makeQuery(id+"F1.opRevolve","SWEPT_FACE",FACE,{"disambiguationData":[OSD([subQ1])]})]});var subQ3=makeQuery(id+"F5.imprint","INTERSECT",VERTEX,{"disambiguationData":[OD(0.0)],"derivedFrom":[subQ2,subQ0]});Q53=makeQuery(id+"F5.imprint","IMPRINT",FACE,{"disambiguationData":[TD([[makeQuery(id+"F5.imprint","IMPRINT",EDGE,{"disambiguationData":[TD([[subQ3,-1.0]])],"derivedFrom":subQ0}),1.0]])]});}
            var Q54;
            {var subQ0=sQuery(id+"F5.wireOp",EDGE,"E11.14.0");var subQ1=sQuery(id+"F5.wireOp",EDGE,"E8.0");var subQ2=makeQuery(id+"F5.imprint","INTERSECT",VERTEX,{"disambiguationData":[OD(0.0)],"derivedFrom":[subQ1,subQ0]});Q54=makeQuery(id+"F5.imprint","IMPRINT",FACE,{"disambiguationData":[TD([[makeQuery(id+"F5.imprint","IMPRINT",EDGE,{"disambiguationData":[TD([[subQ2,-1.0]])],"derivedFrom":subQ1}),1.0]])]});}
            var Q55;
            {var subQ0=sQuery(id+"F5.wireOp",EDGE,"E11.14.0");var subQ1=sQuery(id+"F0.wireOp",EDGE,"E1");var subQ2=makeQuery(id+"F2.opChamfer","BLEND_EDGE",EDGE,{"blendedFrom":[makeQuery(id+"F1.opRevolve","SWEPT_EDGE",EDGE,{"disambiguationData":[OSD([subQ1,sQuery(id+"F0.wireOp",EDGE,"E2")])]}),makeQuery(id+"F1.opRevolve","SWEPT_FACE",FACE,{"disambiguationData":[OSD([subQ1])]})],"blendedInto":[makeQuery(id+"F1.opRevolve","SWEPT_FACE",FACE,{"disambiguationData":[OSD([subQ1])]})]});var subQ3=makeQuery(id+"F5.imprint","INTERSECT",VERTEX,{"disambiguationData":[OD(0.0)],"derivedFrom":[subQ2,subQ0]});Q55=makeQuery(id+"F5.imprint","IMPRINT",FACE,{"disambiguationData":[TD([[makeQuery(id+"F5.imprint","IMPRINT",EDGE,{"disambiguationData":[TD([[subQ3,-1.0]])],"derivedFrom":subQ0}),1.0]])]});}
            var Q56;
            {var subQ0=sQuery(id+"F5.wireOp",EDGE,"E11.15.0");var subQ1=sQuery(id+"F5.wireOp",EDGE,"E8.0");var subQ2=makeQuery(id+"F5.imprint","INTERSECT",VERTEX,{"disambiguationData":[OD(0.0)],"derivedFrom":[subQ1,subQ0]});Q56=makeQuery(id+"F5.imprint","IMPRINT",FACE,{"disambiguationData":[TD([[makeQuery(id+"F5.imprint","IMPRINT",EDGE,{"disambiguationData":[TD([[subQ2,-1.0]])],"derivedFrom":subQ1}),1.0]])]});}
            var Q57;
            {var subQ0=sQuery(id+"F5.wireOp",EDGE,"E11.15.0");var subQ1=sQuery(id+"F0.wireOp",EDGE,"E1");var subQ2=makeQuery(id+"F2.opChamfer","BLEND_EDGE",EDGE,{"blendedFrom":[makeQuery(id+"F1.opRevolve","SWEPT_EDGE",EDGE,{"disambiguationData":[OSD([subQ1,sQuery(id+"F0.wireOp",EDGE,"E2")])]}),makeQuery(id+"F1.opRevolve","SWEPT_FACE",FACE,{"disambiguationData":[OSD([subQ1])]})],"blendedInto":[makeQuery(id+"F1.opRevolve","SWEPT_FACE",FACE,{"disambiguationData":[OSD([subQ1])]})]});var subQ3=makeQuery(id+"F5.imprint","INTERSECT",VERTEX,{"disambiguationData":[OD(0.0)],"derivedFrom":[subQ2,subQ0]});Q57=makeQuery(id+"F5.imprint","IMPRINT",FACE,{"disambiguationData":[TD([[makeQuery(id+"F5.imprint","IMPRINT",EDGE,{"disambiguationData":[TD([[subQ3,-1.0]])],"derivedFrom":subQ0}),1.0]])]});}
            var Q58;
            {var subQ0=sQuery(id+"F5.wireOp",EDGE,"E11.16.0");var subQ1=sQuery(id+"F5.wireOp",EDGE,"E8.0");var subQ2=makeQuery(id+"F5.imprint","INTERSECT",VERTEX,{"disambiguationData":[OD(0.0)],"derivedFrom":[subQ1,subQ0]});Q58=makeQuery(id+"F5.imprint","IMPRINT",FACE,{"disambiguationData":[TD([[makeQuery(id+"F5.imprint","IMPRINT",EDGE,{"disambiguationData":[TD([[subQ2,-1.0]])],"derivedFrom":subQ1}),1.0]])]});}
            var Q59;
            {var subQ0=sQuery(id+"F5.wireOp",EDGE,"E11.16.0");var subQ1=sQuery(id+"F0.wireOp",EDGE,"E1");var subQ2=makeQuery(id+"F2.opChamfer","BLEND_EDGE",EDGE,{"blendedFrom":[makeQuery(id+"F1.opRevolve","SWEPT_EDGE",EDGE,{"disambiguationData":[OSD([subQ1,sQuery(id+"F0.wireOp",EDGE,"E2")])]}),makeQuery(id+"F1.opRevolve","SWEPT_FACE",FACE,{"disambiguationData":[OSD([subQ1])]})],"blendedInto":[makeQuery(id+"F1.opRevolve","SWEPT_FACE",FACE,{"disambiguationData":[OSD([subQ1])]})]});var subQ3=makeQuery(id+"F5.imprint","INTERSECT",VERTEX,{"disambiguationData":[OD(0.0)],"derivedFrom":[subQ2,subQ0]});Q59=makeQuery(id+"F5.imprint","IMPRINT",FACE,{"disambiguationData":[TD([[makeQuery(id+"F5.imprint","IMPRINT",EDGE,{"disambiguationData":[TD([[subQ3,-1.0]])],"derivedFrom":subQ0}),1.0]])]});}
            extrude(context, id + "F6", {"entities" : qUnion([Q0, Q1, Q2, Q3, Q4, Q5, Q6, Q7, Q8, Q9, Q10, Q11, Q12, Q13, Q14, Q15, Q16, Q17, Q18, Q19, Q20, Q21, Q22, Q23, Q24, Q25, Q26, Q27, Q28, Q29, Q30, Q31, Q32, Q33, Q34, Q35, Q36, Q37, Q38, Q39, Q40, Q41, Q42, Q43, Q44, Q45, Q46, Q47, Q48, Q49, Q50, Q51, Q52, Q53, Q54, Q55, Q56, Q57, Q58, Q59]), "operationType" : NewBodyOperationType.REMOVE, "endBound" : BoundingType.THROUGH_ALL, "oppositeDirection" : true, "depth" : 25 * mm});
        }
    });
